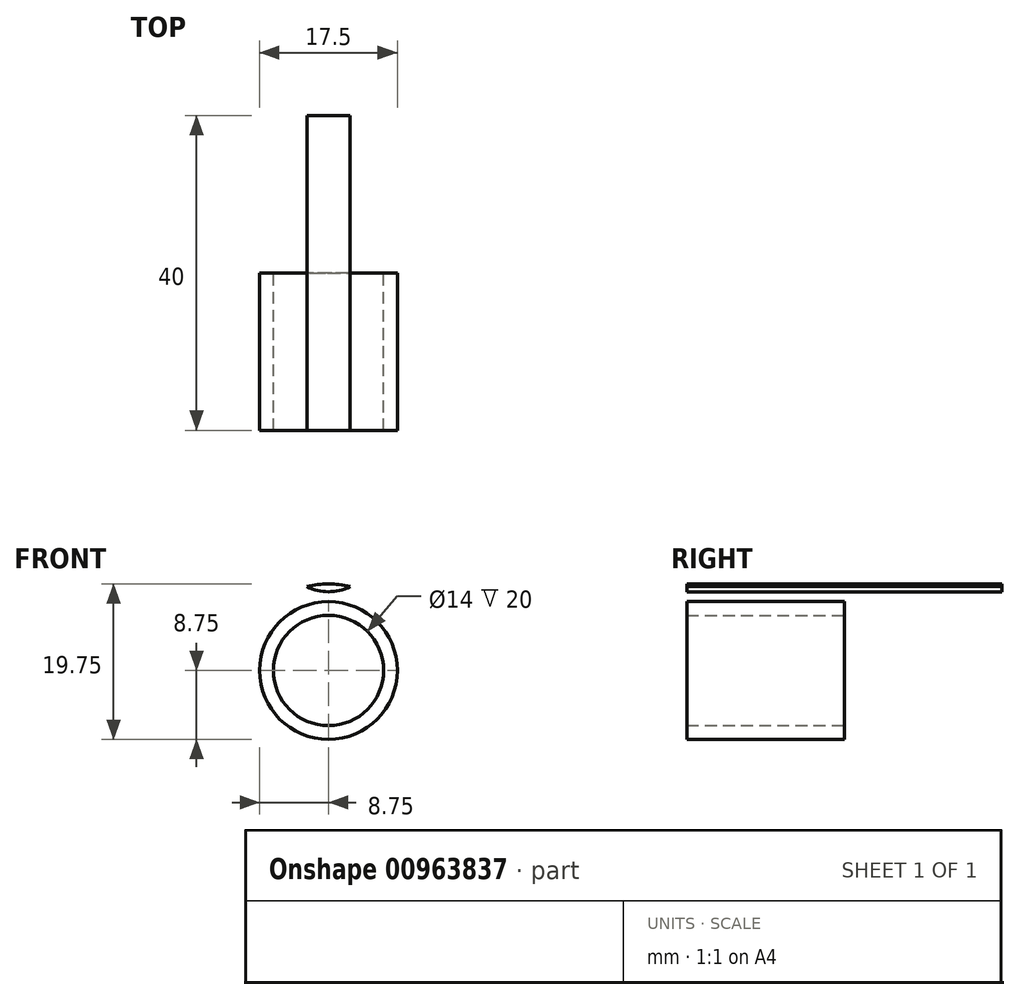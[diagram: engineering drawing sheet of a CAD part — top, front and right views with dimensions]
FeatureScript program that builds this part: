
annotation { "Feature Type Name" : "Feature", "Feature Type Description" : "" }
export const myFeature = defineFeature(function(context is Context, id is Id, definition is map)
    precondition{}
    {
        {
            var Q0;
            Q0=qCreatedBy(makeId("Front.planeOp"),FACE);
            var sketch = newSketch(context, id + "F0", { "sketchPlane" : qUnion([Q0])});
            skCircle(sketch, "E0", {"center": v(0, 0) * mm, "radius": 11 * mm});
            skCircle(sketch, "E1", {"center": v(0, 0) * mm, "radius": 12.5 * mm});
            skCircle(sketch, "E2", {"center": v(0, 16) * mm, "radius": 2.5 * mm});
            skCircle(sketch, "E3", {"center": v(0, 16) * mm, "radius": 6 * mm});
            skLineSegment(sketch, "E4", {"start": v(-5.48, 18.44) * mm, "end": v(-11.42, 5.08) * mm});
            skLineSegment(sketch, "E5", {"start": v(5.48, 18.44) * mm, "end": v(11.42, 5.08) * mm});
            skCircle(sketch, "E6", {"center": v(0, 0) * mm, "radius": 8.75 * mm});
            skCircle(sketch, "E7", {"center": v(0, 0) * mm, "radius": 7 * mm});
            skSolve(sketch);
        }
        {
            var Q0;
            {var subQ0=sQuery(id+"F0.wireOp",EDGE,"E3");var subQ1=sQuery(id+"F0.wireOp",EDGE,"E0");var subQ2=makeQuery(id+"F0.imprint","INTERSECT",VERTEX,{"disambiguationData":[OD(0.0)],"derivedFrom":[subQ1,subQ0]});Q0=makeQuery(id+"F0.imprint","IMPRINT",FACE,{"disambiguationData":[TD([[makeQuery(id+"F0.imprint","IMPRINT",EDGE,{"disambiguationData":[TD([[subQ2,-1.0]])],"derivedFrom":subQ1}),1.0]])]});}
            var Q1;
            Q1=makeQuery(id+"F0.imprint","IMPRINT",FACE,{"disambiguationData":[TD([[makeQuery(id+"F0.imprint","IMPRINT",EDGE,{"derivedFrom":sQuery(id+"F0.wireOp",EDGE,"E6")}),1.0]])]});
            extrude(context, id + "F1", {"entities" : qUnion([Q0, Q1]), "depth" : 40 * mm, "offsetDistance" : 25 * mm});
        }
        {
            var Q0;
            Q0=makeQuery(id+"F0.imprint","IMPRINT",FACE,{"disambiguationData":[TD([[makeQuery(id+"F0.imprint","IMPRINT",EDGE,{"derivedFrom":sQuery(id+"F0.wireOp",EDGE,"E6")}),1.0]])]});
            var Q1;
            Q1=sQuery(id+"F0.wireOp",EDGE,"E6");
            extrude(context, id + "F2", {"entities" : qUnion([Q0]), "operationType" : NewBodyOperationType.REMOVE, "surfaceEntities" : qUnion([Q1]), "depth" : 20 * mm, "offsetDistance" : 25 * mm});
        }
    });
